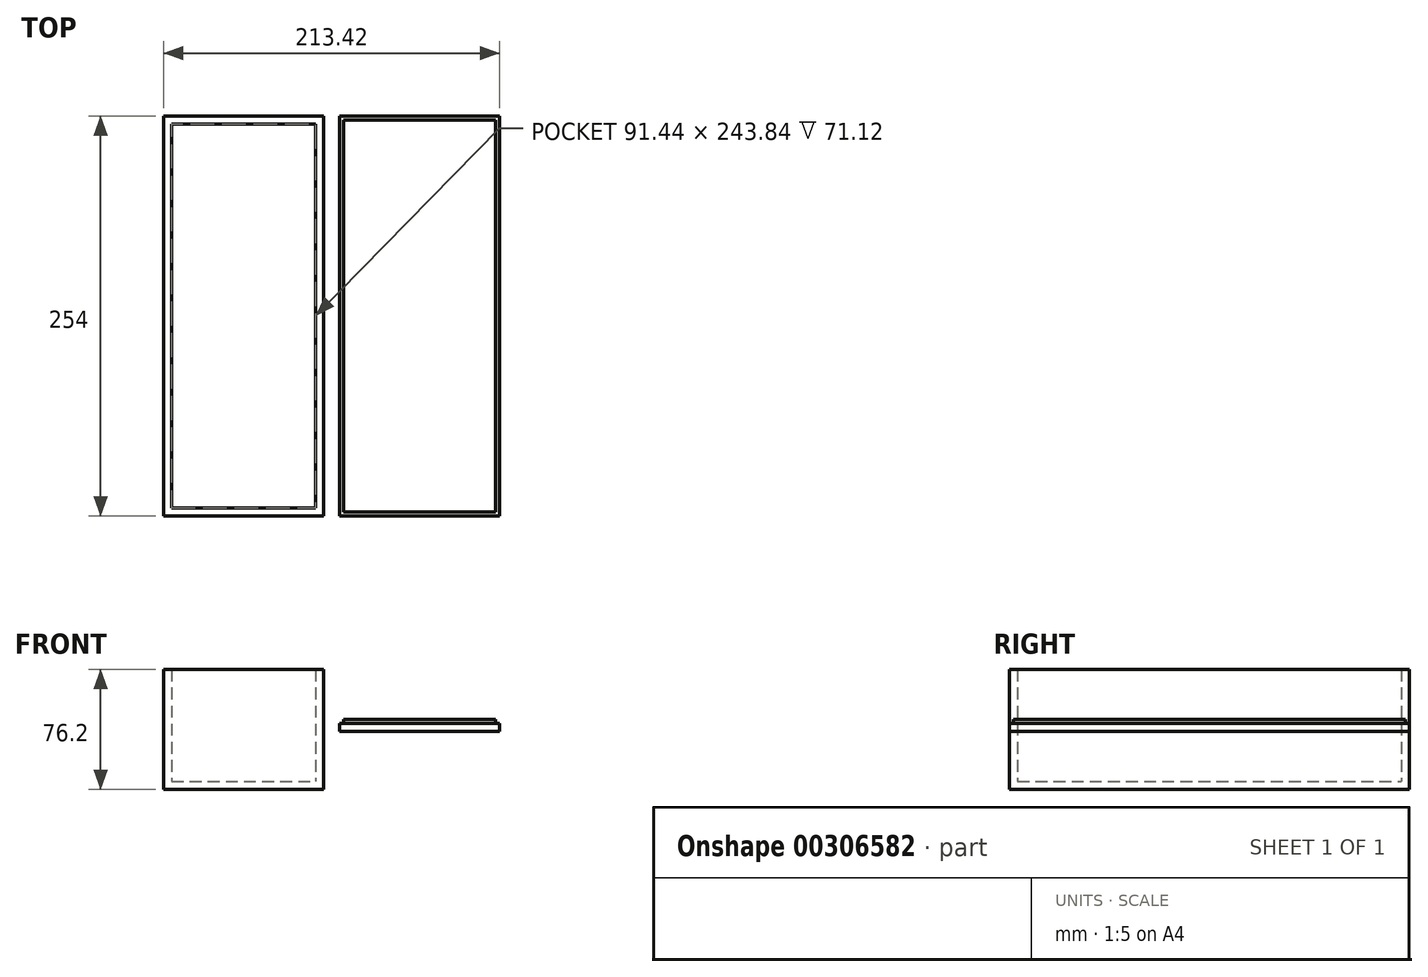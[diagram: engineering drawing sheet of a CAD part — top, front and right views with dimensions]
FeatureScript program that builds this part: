
annotation { "Feature Type Name" : "Feature", "Feature Type Description" : "" }
export const myFeature = defineFeature(function(context is Context, id is Id, definition is map)
    precondition{}
    {
        {
            var Q0;
            Q0=qCreatedBy(makeId("Front.planeOp"),FACE);
            var sketch = newSketch(context, id + "F0", { "sketchPlane" : qUnion([Q0])});
            skLineSegment(sketch, "E0.bottom", {"start": v(-52.15, 39.24) * mm, "end": v(49.45, 39.24) * mm});
            skLineSegment(sketch, "E0.top", {"start": v(-52.15, -36.96) * mm, "end": v(49.45, -36.96) * mm});
            skLineSegment(sketch, "E0.left", {"start": v(-52.15, 39.24) * mm, "end": v(-52.15, -36.96) * mm});
            skLineSegment(sketch, "E0.right", {"start": v(49.45, 39.24) * mm, "end": v(49.45, -36.96) * mm});
            skSolve(sketch);
        }
        {
            var Q0;
            Q0 = qSketchRegion(id + "F0", true);
            extrude(context, id + "F1", {"entities" : qUnion([Q0]), "depth" : 254 * mm});
        }
        {
            var Q0;
            Q0=makeQuery(id+"F1.opExtrude","SWEPT_FACE",FACE,{"disambiguationData":[OSD([sQuery(id+"F0.wireOp",EDGE,"E0.bottom")])]});
            shell(context, id + "F2", {"entities" : qUnion([Q0]), "thickness" : 5.08 * mm});
        }
        {
            var Q0;
            Q0=qCreatedBy(makeId("Top.planeOp"),FACE);
            var sketch = newSketch(context, id + "F3", { "sketchPlane" : qUnion([Q0])});
            skLineSegment(sketch, "E1.bottom", {"start": v(59.67, 0) * mm, "end": v(161.27, 0) * mm});
            skLineSegment(sketch, "E1.top", {"start": v(59.67, -254) * mm, "end": v(161.27, -254) * mm});
            skLineSegment(sketch, "E1.left", {"start": v(59.67, 0) * mm, "end": v(59.67, -254) * mm});
            skLineSegment(sketch, "E1.right", {"start": v(161.27, 0) * mm, "end": v(161.27, -254) * mm});
            skSolve(sketch);
        }
        {
            var Q0;
            Q0=makeQuery(id+"F3.imprint","IMPRINT",FACE,{"disambiguationData":[TD([[makeQuery(id+"F3.imprint","IMPRINT",EDGE,{"derivedFrom":sQuery(id+"F3.wireOp",EDGE,"E1.bottom")}),-1.0]])]});
            extrude(context, id + "F4", {"entities" : qUnion([Q0]), "depth" : 5.08 * mm});
        }
        {
            var Q0;
            Q0=makeQuery(id+"F4.opExtrude","CAP_FACE",FACE,{"disambiguationData":[OSD([sQuery(id+"F3.wireOp",EDGE,"E1.bottom"),sQuery(id+"F3.wireOp",EDGE,"E1.top"),sQuery(id+"F3.wireOp",EDGE,"E1.left"),sQuery(id+"F3.wireOp",EDGE,"E1.right")])],"isStart":false});
            var sketch = newSketch(context, id + "F5", { "sketchPlane" : qUnion([Q0])});
            skLineSegment(sketch, "E2.bottom", {"start": v(158.58, -251.54) * mm, "end": v(62.06, -251.54) * mm});
            skLineSegment(sketch, "E2.top", {"start": v(158.58, -2.62) * mm, "end": v(62.06, -2.62) * mm});
            skLineSegment(sketch, "E2.left", {"start": v(158.58, -251.54) * mm, "end": v(158.58, -2.62) * mm});
            skLineSegment(sketch, "E2.right", {"start": v(62.06, -251.54) * mm, "end": v(62.06, -2.62) * mm});
            skSolve(sketch);
        }
        {
            var Q0;
            Q0 = qSketchRegion(id + "F5", true);
            extrude(context, id + "F6", {"entities" : qUnion([Q0]), "operationType" : NewBodyOperationType.ADD, "depth" : 2.54 * mm});
        }
    });
